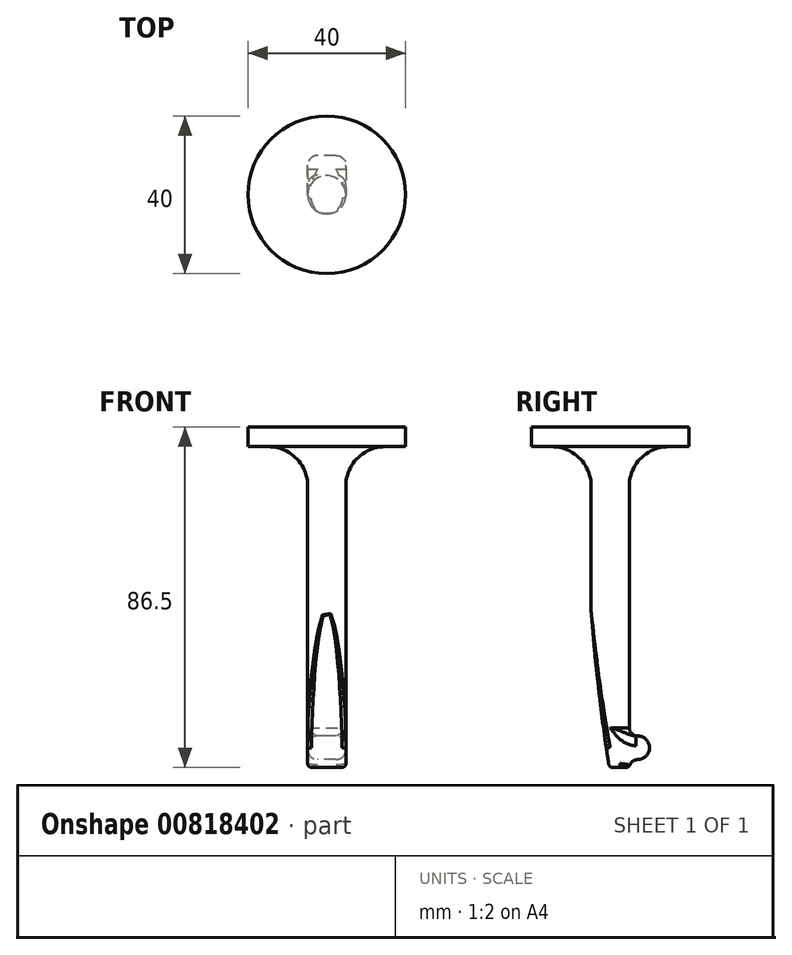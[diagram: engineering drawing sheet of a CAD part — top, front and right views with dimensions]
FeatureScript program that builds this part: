
annotation { "Feature Type Name" : "Feature", "Feature Type Description" : "" }
export const myFeature = defineFeature(function(context is Context, id is Id, definition is map)
    precondition{}
    {
        {
            assignVariable(context, id + "F0", {"name" : "Daxe", "anyValue" : 9.7});
        }
        {
            var Q0;
            Q0=qCreatedBy(makeId("Front.planeOp"),FACE);
            var sketch = newSketch(context, id + "F1", { "sketchPlane" : qUnion([Q0])});
            skLineSegment(sketch, "E0", {"start": v(-4.85, 81.5) * mm, "end": v(-20, 81.5) * mm});
            skLineSegment(sketch, "E1", {"start": v(-20, 81.5) * mm, "end": v(-20, 86.5) * mm});
            skLineSegment(sketch, "E2", {"start": v(-20, 86.5) * mm, "end": v(0, 86.5) * mm});
            skLineSegment(sketch, "E3", {"start": v(0, 86.5) * mm, "end": v(0, 0) * mm});
            skLineSegment(sketch, "E4", {"start": v(0, 0) * mm, "end": v(-4.85, 0) * mm});
            skLineSegment(sketch, "E5", {"start": v(-4.85, 0) * mm, "end": v(-4.85, 81.5) * mm});
            skSolve(sketch);
        }
        {
            var Q0;
            Q0=makeQuery(id+"F1.imprint","IMPRINT",FACE,{"disambiguationData":[TD([[makeQuery(id+"F1.imprint","IMPRINT",EDGE,{"derivedFrom":sQuery(id+"F1.wireOp",EDGE,"E0")}),-1.0]])]});
            var Q1;
            Q1=sQuery(id+"F1.wireOp",EDGE,"E3");
            revolve(context, id + "F2", {"surfaceOperationType" : NewSurfaceOperationType.NEW, "entities" : qUnion([Q0]), "axis" : qUnion([Q1]), "revolveType" : RevolveType.FULL});
        }
        {
            var Q0;
            Q0=qCreatedBy(makeId("Right.planeOp"),FACE);
            var sketch = newSketch(context, id + "F3", { "sketchPlane" : qUnion([Q0])});
            skArc(sketch, "E6", {"start": v(4.85, 10) * mm, "mid": v(5.53, 8.58) * mm, "end": v(7, 8) * mm});
            skArc(sketch, "E7", {"start": v(10, 5) * mm, "mid": v(9.12, 7.12) * mm, "end": v(7, 8) * mm});
            skLineSegment(sketch, "E8", {"start": v(0, 5) * mm, "end": v(10, 5) * mm, "construction": true});
            skLineSegment(sketch, "E9", {"start": v(4.85, 89) * mm, "end": v(4.85, 0) * mm, "construction": true});
            skLineSegment(sketch, "E10", {"start": v(-4.85, 0) * mm, "end": v(-4.85, 89) * mm, "construction": true});
            skArc(sketch, "E11.MirrorCS", {"start": v(10, 5) * mm, "mid": v(9.12, 2.88) * mm, "end": v(7, 2) * mm});
            skArc(sketch, "E12.MirrorCS", {"start": v(4.85, 0) * mm, "mid": v(5.53, 1.42) * mm, "end": v(7, 2) * mm});
            skLineSegment(sketch, "E13", {"start": v(4.85, 10) * mm, "end": v(0, 10) * mm});
            skLineSegment(sketch, "E14", {"start": v(0, 10) * mm, "end": v(0, 0) * mm});
            skLineSegment(sketch, "E15", {"start": v(0, 0) * mm, "end": v(4.85, 0) * mm});
            skSolve(sketch);
        }
        {
            var Q0;
            Q0=makeQuery(id+"F3.imprint","IMPRINT",FACE,{"disambiguationData":[TD([[makeQuery(id+"F3.imprint","IMPRINT",EDGE,{"derivedFrom":sQuery(id+"F3.wireOp",EDGE,"E6")}),-1.0]])]});
            extrude(context, id + "F4", {"entities" : qUnion([Q0]), "operationType" : NewBodyOperationType.ADD, "endBound" : BoundingType.SYMMETRIC, "depth" : (getVariable(context, 'Daxe')) * mm, "offsetDistance" : 25 * mm});
        }
        {
            var Q0;
            Q0=qCreatedBy(makeId("Right.planeOp"),FACE);
            var sketch = newSketch(context, id + "F5", { "sketchPlane" : qUnion([Q0])});
            skArc(sketch, "E16.0", {"start": v(4.85, 10) * mm, "mid": v(5.53, 8.58) * mm, "end": v(7, 8) * mm});
            skArc(sketch, "E17.0", {"start": v(4.85, 0) * mm, "mid": v(5.53, 1.42) * mm, "end": v(7, 2) * mm});
            skLineSegment(sketch, "E18", {"start": v(14.85, 0) * mm, "end": v(4.85, 0) * mm});
            skLineSegment(sketch, "E19", {"start": v(0, 0) * mm, "end": v(0, 12.7) * mm, "construction": true});
            skLineSegment(sketch, "E20", {"start": v(4.85, 10) * mm, "end": v(14.85, 10) * mm});
            skLineSegment(sketch, "E21", {"start": v(14.85, 10) * mm, "end": v(14.85, 8) * mm});
            skLineSegment(sketch, "E22", {"start": v(14.85, 8) * mm, "end": v(7, 8) * mm});
            skLineSegment(sketch, "E23", {"start": v(14.85, 0) * mm, "end": v(14.85, 2) * mm});
            skLineSegment(sketch, "E24", {"start": v(14.85, 2) * mm, "end": v(7, 2) * mm});
            skSolve(sketch);
        }
        {
            var Q0;
            Q0=makeQuery(id+"F5.imprint","IMPRINT",FACE,{"disambiguationData":[TD([[makeQuery(id+"F5.imprint","IMPRINT",EDGE,{"derivedFrom":sQuery(id+"F5.wireOp",EDGE,"E16.0")}),1.0]])]});
            var Q1;
            Q1=makeQuery(id+"F5.imprint","IMPRINT",FACE,{"disambiguationData":[TD([[makeQuery(id+"F5.imprint","IMPRINT",EDGE,{"derivedFrom":sQuery(id+"F5.wireOp",EDGE,"E17.0")}),-1.0]])]});
            var Q2;
            Q2=sQuery(id+"F5.wireOp",EDGE,"E19");
            revolve(context, id + "F6", {"operationType" : NewBodyOperationType.REMOVE, "surfaceOperationType" : NewSurfaceOperationType.NEW, "entities" : qUnion([Q0, Q1]), "axis" : qUnion([Q2]), "revolveType" : RevolveType.FULL, "oppositeDirection" : true});
        }
        {
            var Q0;
            Q0=makeQuery(id+"F4.opExtrude","CAP_EDGE",EDGE,{"disambiguationData":[OSD([sQuery(id+"F3.wireOp",EDGE,"E6")])],"isStart":false});
            var Q1;
            Q1=makeQuery(id+"F4.opExtrude","CAP_EDGE",EDGE,{"disambiguationData":[OSD([sQuery(id+"F3.wireOp",EDGE,"E7"),sQuery(id+"F3.wireOp",EDGE,"E11.MirrorCS")])],"isStart":false});
            var Q2;
            Q2=makeQuery(id+"F4.opExtrude","CAP_EDGE",EDGE,{"disambiguationData":[OSD([sQuery(id+"F3.wireOp",EDGE,"E6")])],"isStart":true});
            var Q3;
            Q3=makeQuery(id+"F4.opExtrude","CAP_EDGE",EDGE,{"disambiguationData":[OSD([sQuery(id+"F3.wireOp",EDGE,"E7"),sQuery(id+"F3.wireOp",EDGE,"E11.MirrorCS")])],"isStart":true});
            fillet(context, id + "F7", {"entities" : qUnion([Q0, Q1, Q2, Q3]), "radius" : 2.5 * mm, "tangentPropagation" : true, "allowEdgeOverflow" : false});
        }
        {
            var Q0;
            Q0=makeQuery(id+"F2.opRevolve","SWEPT_EDGE",EDGE,{"disambiguationData":[OSD([sQuery(id+"F1.wireOp",EDGE,"E0"),sQuery(id+"F1.wireOp",EDGE,"E5")])]});
            fillet(context, id + "F8", {"entities" : qUnion([Q0]), "radius" : 10 * mm, "tangentPropagation" : true, "allowEdgeOverflow" : false});
        }
        {
            var Q0;
            Q0=qCreatedBy(makeId("Right.planeOp"),FACE);
            var sketch = newSketch(context, id + "F9", { "sketchPlane" : qUnion([Q0])});
            skArc(sketch, "E25", {"start": v(5.4, 8.71) * mm, "mid": v(6.12, 8.19) * mm, "end": v(7, 8) * mm});
            skArc(sketch, "E26", {"start": v(7, 2) * mm, "mid": v(10, 5) * mm, "end": v(7, 8) * mm});
            skArc(sketch, "E27", {"start": v(7, 2) * mm, "mid": v(6.12, 1.81) * mm, "end": v(5.4, 1.29) * mm});
            skArc(sketch, "E28", {"start": v(4.85, 9.99) * mm, "mid": v(5.54, 8.57) * mm, "end": v(7, 8) * mm, "construction": true});
            skArc(sketch, "E29", {"start": v(7, 2) * mm, "mid": v(5.54, 1.43) * mm, "end": v(4.85, 0.01) * mm, "construction": true});
            skSolve(sketch);
        }
        {
            var Q0;
            Q0=qCreatedBy(makeId("Right.planeOp"),FACE);
            var sketch = newSketch(context, id + "F10", { "sketchPlane" : qUnion([Q0])});
            skArc(sketch, "E30", {"start": v(-4.85, 40) * mm, "mid": v(-2.94, 19.96) * mm, "end": v(-0.25, 0) * mm});
            skLineSegment(sketch, "E31", {"start": v(-4.85, 0) * mm, "end": v(-4.85, 71.5) * mm, "construction": true});
            skLineSegment(sketch, "E32", {"start": v(4.85, 71.5) * mm, "end": v(4.85, 10.54) * mm, "construction": true});
            skLineSegment(sketch, "E33", {"start": v(-1, 5) * mm, "end": v(10, 5) * mm, "construction": true});
            skLineSegment(sketch, "E34", {"start": v(-4.85, 0) * mm, "end": v(-0.25, 0) * mm});
            skLineSegment(sketch, "E35", {"start": v(-4.85, 0) * mm, "end": v(-4.85, 40) * mm});
            skPoint(sketch, "E36", {"position": v(-4.85, 35.75) * mm});
            skSolve(sketch);
        }
        {
            var Q0;
            Q0=qSketchRegion(id+"F10",true);
            extrude(context, id + "F11", {"entities" : qUnion([Q0]), "operationType" : NewBodyOperationType.REMOVE, "endBound" : BoundingType.SYMMETRIC, "oppositeDirection" : true, "depth" : 10 * mm, "offsetDistance" : 25 * mm});
        }
        {
            var Q0;
            Q0=makeQuery(id+"F11.boolean.opBoolean","INTERSECT",EDGE,{"disambiguationData":[OD(1.0)],"derivedFrom":[makeQuery(id+"F2.opRevolve","SWEPT_FACE",FACE,{"disambiguationData":[OSD([sQuery(id+"F1.wireOp",EDGE,"E5")])]}),makeQuery(id+"F11.opExtrude","SWEPT_FACE",FACE,{"disambiguationData":[OSD([sQuery(id+"F10.wireOp",EDGE,"E30")])]})]});
            var Q1;
            Q1=makeQuery(id+"F11.boolean.opBoolean","INTERSECT",EDGE,{"disambiguationData":[OD(0.0)],"derivedFrom":[makeQuery(id+"F2.opRevolve","SWEPT_FACE",FACE,{"disambiguationData":[OSD([sQuery(id+"F1.wireOp",EDGE,"E5")])]}),makeQuery(id+"F11.opExtrude","SWEPT_FACE",FACE,{"disambiguationData":[OSD([sQuery(id+"F10.wireOp",EDGE,"E30")])]})]});
            fillet(context, id + "F12", {"entities" : qUnion([Q0, Q1]), "radius" : 1 * mm, "tangentPropagation" : true, "allowEdgeOverflow" : false});
        }
        {
            var Q0;
            Q0=makeQuery(id+"F12.opFillet","BLEND_EDGE",EDGE,{"blendedFrom":[makeQuery(id+"F11.boolean.opBoolean","INTERSECT",EDGE,{"disambiguationData":[OD(1.0)],"derivedFrom":[makeQuery(id+"F2.opRevolve","SWEPT_FACE",FACE,{"disambiguationData":[OSD([sQuery(id+"F1.wireOp",EDGE,"E5")])]}),makeQuery(id+"F11.opExtrude","SWEPT_FACE",FACE,{"disambiguationData":[OSD([sQuery(id+"F10.wireOp",EDGE,"E30")])]})]}),makeQuery(id+"F4.boolean.opBoolean","MERGE",FACE,{"derivedFrom":[makeQuery(id+"F2.opRevolve","SWEPT_FACE",FACE,{"disambiguationData":[OSD([sQuery(id+"F1.wireOp",EDGE,"E4")])]}),makeQuery(id+"F4.opExtrude","SWEPT_FACE",FACE,{"disambiguationData":[OSD([sQuery(id+"F3.wireOp",EDGE,"E15")])]})]})],"blendedInto":[makeQuery(id+"F4.boolean.opBoolean","MERGE",FACE,{"derivedFrom":[makeQuery(id+"F2.opRevolve","SWEPT_FACE",FACE,{"disambiguationData":[OSD([sQuery(id+"F1.wireOp",EDGE,"E4")])]}),makeQuery(id+"F4.opExtrude","SWEPT_FACE",FACE,{"disambiguationData":[OSD([sQuery(id+"F3.wireOp",EDGE,"E15")])]})]})]});
            fillet(context, id + "F13", {"entities" : qUnion([Q0]), "radius" : 1 * mm, "tangentPropagation" : true, "allowEdgeOverflow" : false});
        }
    });
